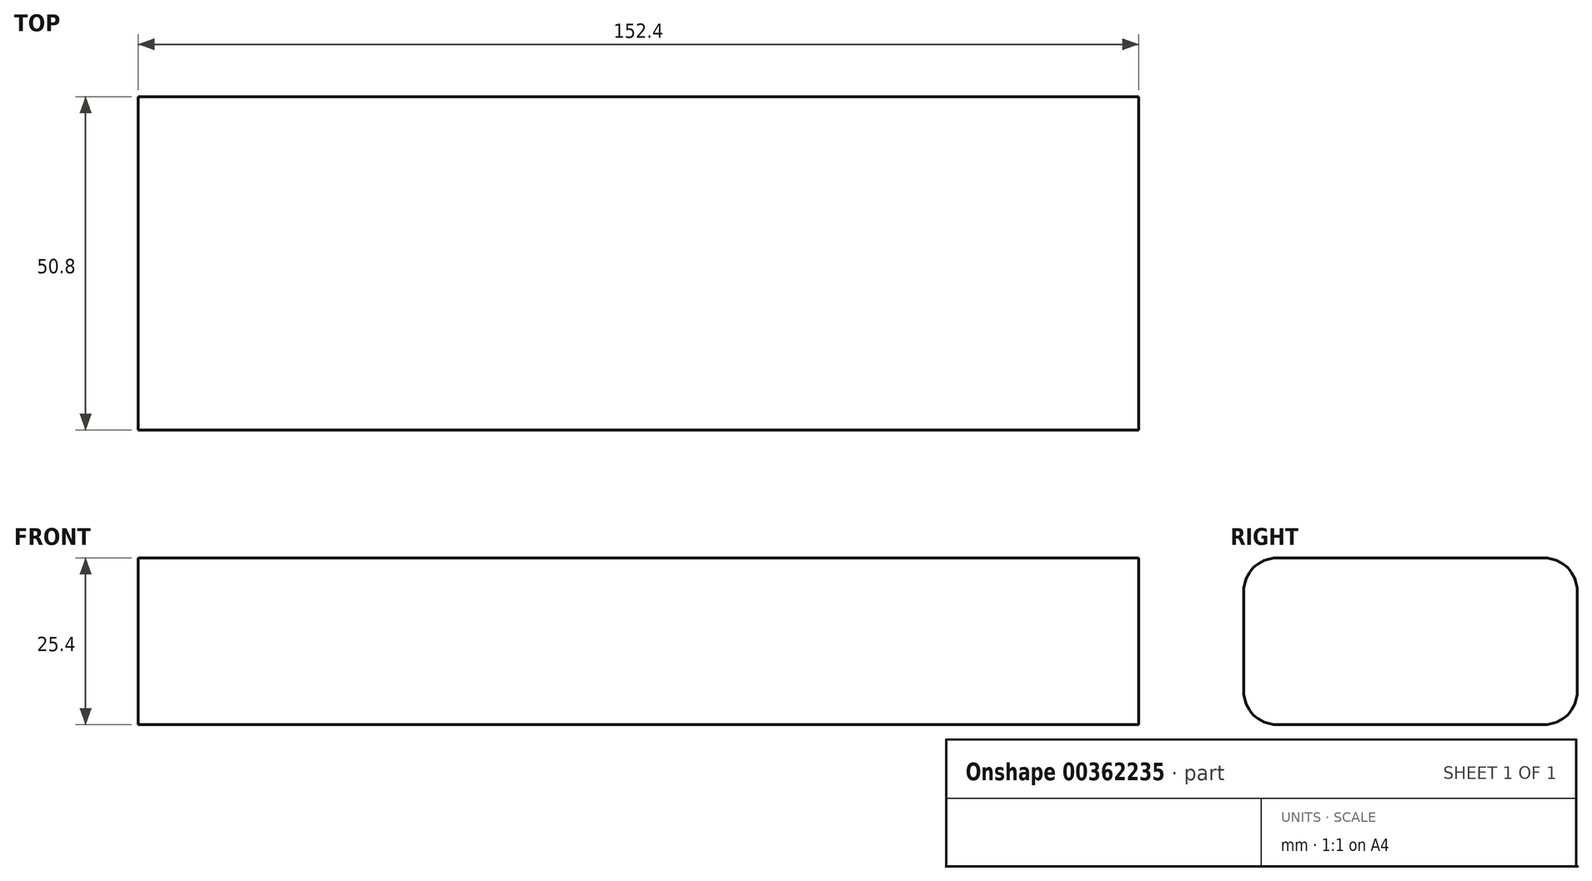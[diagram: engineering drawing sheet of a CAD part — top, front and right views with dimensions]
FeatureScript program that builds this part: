
annotation { "Feature Type Name" : "Feature", "Feature Type Description" : "" }
export const myFeature = defineFeature(function(context is Context, id is Id, definition is map)
    precondition{}
    {
        {
            var Q0;
            Q0=qCreatedBy(makeId("Front.planeOp"),FACE);
            var sketch = newSketch(context, id + "F0", { "sketchPlane" : qUnion([Q0])});
            skLineSegment(sketch, "E0.bottom", {"start": v(-76.2, 12.7) * mm, "end": v(76.2, 12.7) * mm});
            skLineSegment(sketch, "E0.top", {"start": v(-76.2, -12.7) * mm, "end": v(76.2, -12.7) * mm});
            skLineSegment(sketch, "E0.left", {"start": v(-76.2, 12.7) * mm, "end": v(-76.2, -12.7) * mm});
            skLineSegment(sketch, "E0.right", {"start": v(76.2, 12.7) * mm, "end": v(76.2, -12.7) * mm});
            skPoint(sketch, "E0.middle", {"position": v(0, 0) * mm});
            skSolve(sketch);
        }
        {
            var Q0;
            Q0=makeQuery(id+"F0.imprint","IMPRINT",FACE,{"disambiguationData":[TD([[makeQuery(id+"F0.imprint","IMPRINT",EDGE,{"derivedFrom":sQuery(id+"F0.wireOp",EDGE,"E0.bottom")}),-1.0]])]});
            extrude(context, id + "F1", {"entities" : qUnion([Q0]), "endBound" : BoundingType.SYMMETRIC, "depth" : 25.4 * mm});
        }
        {
            var Q0;
            Q0=makeQuery(id+"F1.opExtrude","CAP_FACE",FACE,{"disambiguationData":[OSD([sQuery(id+"F0.wireOp",EDGE,"E0.bottom"),sQuery(id+"F0.wireOp",EDGE,"E0.top"),sQuery(id+"F0.wireOp",EDGE,"E0.left"),sQuery(id+"F0.wireOp",EDGE,"E0.right")])],"isStart":false});
            extrude(context, id + "F2", {"entities" : qUnion([Q0]), "operationType" : NewBodyOperationType.ADD, "depth" : 25.4 * mm});
        }
        {
            var Q0;
            Q0=makeQuery(id+"F2.opExtrude","CAP_EDGE",EDGE,{"disambiguationData":[OSD([sQuery(id+"F0.wireOp",EDGE,"E0.bottom")])],"isStart":false});
            var Q1;
            Q1=makeQuery(id+"F2.opExtrude","CAP_EDGE",EDGE,{"disambiguationData":[OSD([sQuery(id+"F0.wireOp",EDGE,"E0.top")])],"isStart":false});
            var Q2;
            Q2=makeQuery(id+"F1.opExtrude","CAP_EDGE",EDGE,{"disambiguationData":[OSD([sQuery(id+"F0.wireOp",EDGE,"E0.bottom")])],"isStart":true});
            var Q3;
            Q3=makeQuery(id+"F1.opExtrude","CAP_EDGE",EDGE,{"disambiguationData":[OSD([sQuery(id+"F0.wireOp",EDGE,"E0.top")])],"isStart":true});
            fillet(context, id + "F3", {"entities" : qUnion([Q0, Q1, Q2, Q3]), "radius" : 5.08 * mm, "tangentPropagation" : true, "allowEdgeOverflow" : false});
        }
    });
